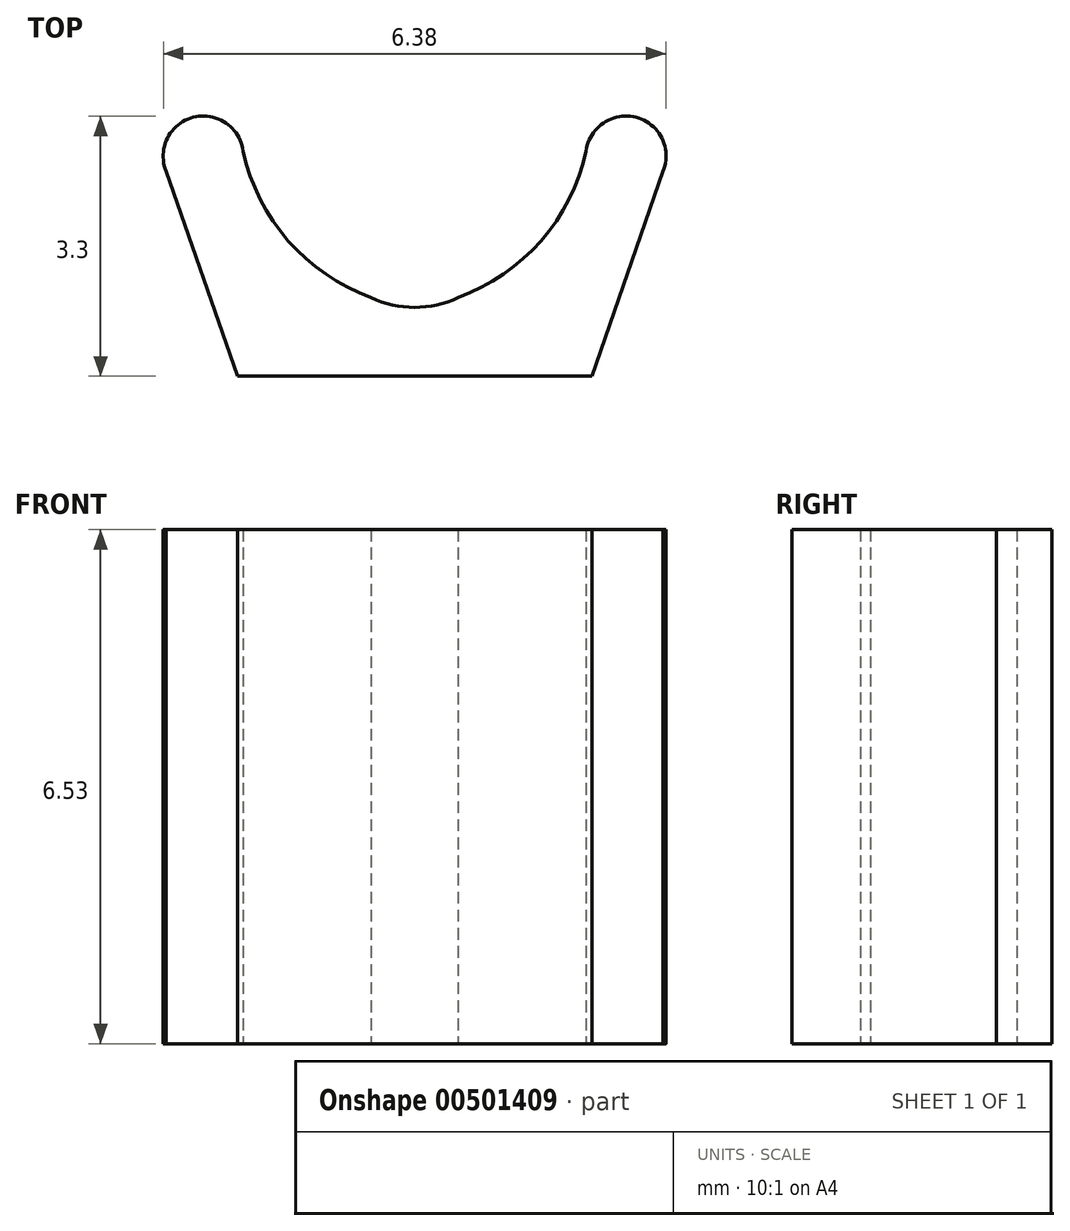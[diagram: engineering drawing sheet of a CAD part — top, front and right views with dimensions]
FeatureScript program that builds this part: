
annotation { "Feature Type Name" : "Feature", "Feature Type Description" : "" }
export const myFeature = defineFeature(function(context is Context, id is Id, definition is map)
    precondition{}
    {
        {
            var Q0;
            Q0=qCreatedBy(makeId("Top.planeOp"),FACE);
            var sketch = newSketch(context, id + "F0", { "sketchPlane" : qUnion([Q0])});
            skLineSegment(sketch, "E0", {"start": v(-13, 0) * mm, "end": v(12.33, 0) * mm, "construction": true});
            skLineSegment(sketch, "E1", {"start": v(0, 11.04) * mm, "end": v(0, -12.7) * mm, "construction": true});
            skLineSegment(sketch, "E2", {"start": v(0, 0) * mm, "end": v(-2.25, 0) * mm});
            skLineSegment(sketch, "E3", {"start": v(-2.25, 0) * mm, "end": v(-3.17, 2.65) * mm});
            skLineSegment(sketch, "E4", {"start": v(-2.75, 3.3) * mm, "end": v(-2.62, 3.3) * mm});
            skLineSegment(sketch, "E5.MirrorCS", {"start": v(0, 0) * mm, "end": v(2.25, 0) * mm});
            skArc(sketch, "E6", {"start": v(-2.2, 2.93) * mm, "mid": v(-1.63, 1.75) * mm, "end": v(-0.55, 1) * mm});
            skArc(sketch, "E7", {"start": v(-2.18, 2.86) * mm, "mid": v(-2.81, 3.29) * mm, "end": v(-3.16, 2.6) * mm});
            skPoint(sketch, "E8.orphan", {"position": v(-3.4, 3.3) * mm});
            skPoint(sketch, "E9.MirrorCS.start.orphan", {"position": v(2.25, 0) * mm});
            skArc(sketch, "E10.MirrorCS", {"start": v(2.2, 2.93) * mm, "mid": v(1.63, 1.75) * mm, "end": v(0.55, 1) * mm});
            skArc(sketch, "E11.MirrorCS", {"start": v(2.18, 2.86) * mm, "mid": v(2.81, 3.29) * mm, "end": v(3.16, 2.6) * mm});
            skLineSegment(sketch, "E12.MirrorCS", {"start": v(2.25, 0) * mm, "end": v(3.17, 2.65) * mm});
            skArc(sketch, "E13", {"start": v(-0.55, 1) * mm, "mid": v(0, 0.87) * mm, "end": v(0.55, 1) * mm});
            skPoint(sketch, "E14.trimOffspring.end.orphan", {"position": v(0, 0.87) * mm});
            skSolve(sketch);
        }
        {
            var Q0;
            Q0 = qSketchRegion(id + "F0", true);
            extrude(context, id + "F1", {"entities" : qUnion([Q0]), "depth" : 6.53 * mm, "offsetDistance" : 25 * mm});
        }
    });
